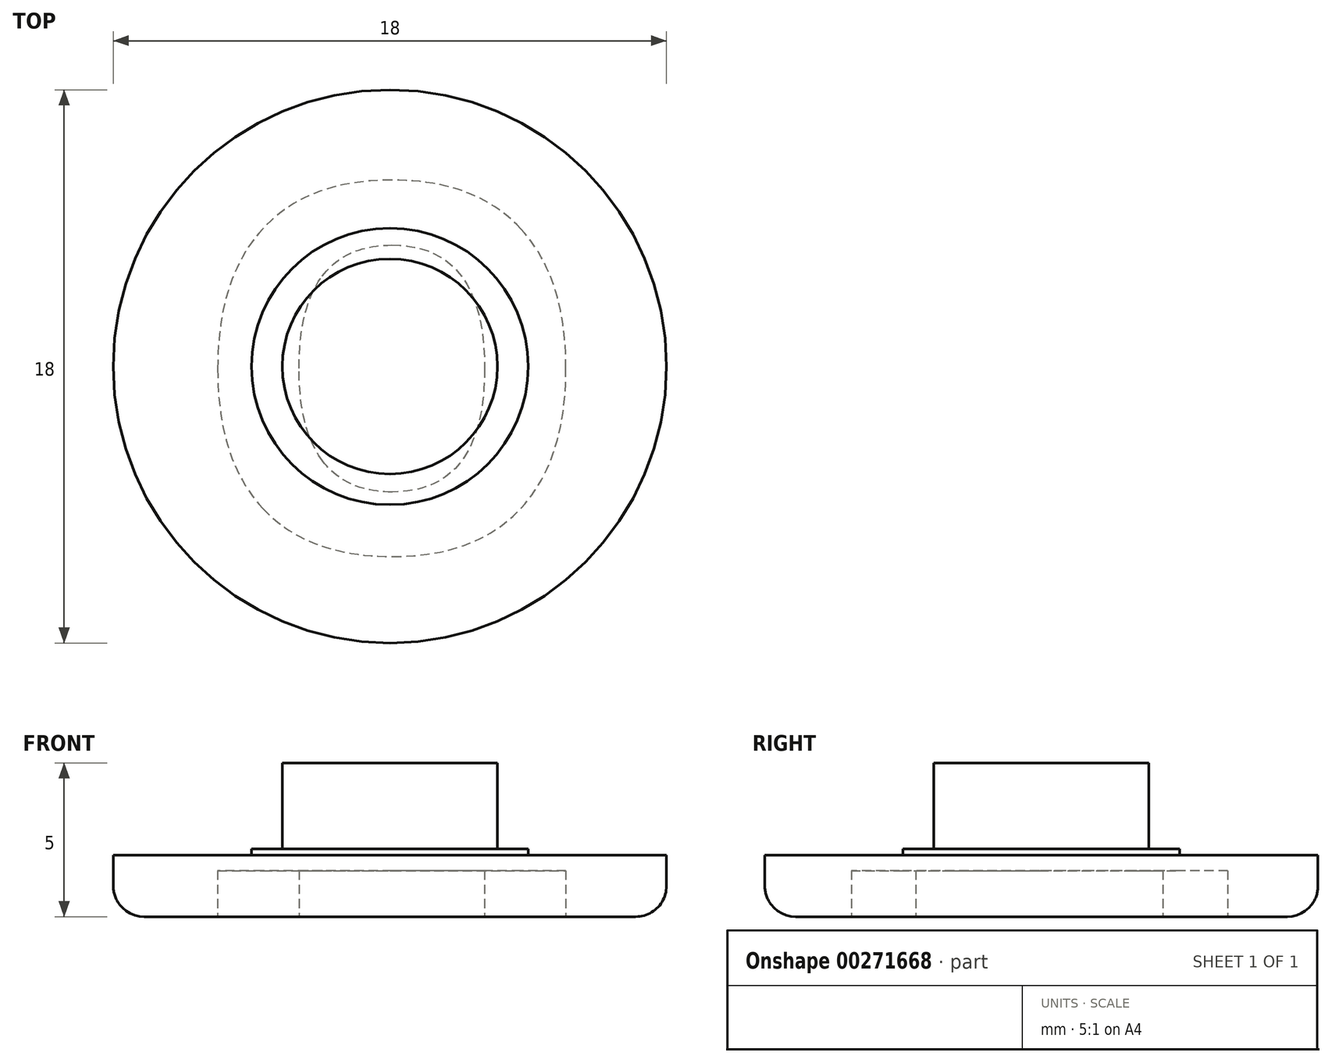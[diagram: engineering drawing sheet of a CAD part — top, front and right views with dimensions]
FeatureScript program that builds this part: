
annotation { "Feature Type Name" : "Feature", "Feature Type Description" : "" }
export const myFeature = defineFeature(function(context is Context, id is Id, definition is map)
    precondition{}
    {
        {
            var Q0;
            Q0=qCreatedBy(makeId("Top.planeOp"),FACE);
            var sketch = newSketch(context, id + "F0", { "sketchPlane" : qUnion([Q0])});
            skCircle(sketch, "E0", {"center": v(0, 0) * mm, "radius": 9 * mm});
            skSolve(sketch);
        }
        {
            var Q0;
            Q0=makeQuery(id+"F0.imprint","IMPRINT",FACE,{"disambiguationData":[TD([[makeQuery(id+"F0.imprint","IMPRINT",EDGE,{"derivedFrom":sQuery(id+"F0.wireOp",EDGE,"E0")}),1.0]])]});
            extrude(context, id + "F1", {"entities" : qUnion([Q0]), "depth" : 2 * mm});
        }
        {
            var Q0;
            Q0=makeQuery(id+"F1.opExtrude","CAP_FACE",FACE,{"disambiguationData":[OSD([sQuery(id+"F0.wireOp",EDGE,"E0")])],"isStart":false});
            var sketch = newSketch(context, id + "F2", { "sketchPlane" : qUnion([Q0])});
            skCircle(sketch, "E1", {"center": v(0, 0) * mm, "radius": 3.5 * mm});
            skSolve(sketch);
        }
        {
            var Q0;
            Q0=makeQuery(id+"F2.imprint","IMPRINT",FACE,{"disambiguationData":[TD([[makeQuery(id+"F2.imprint","IMPRINT",EDGE,{"derivedFrom":sQuery(id+"F2.wireOp",EDGE,"E1")}),1.0]])]});
            extrude(context, id + "F3", {"entities" : qUnion([Q0]), "operationType" : NewBodyOperationType.ADD, "depth" : 3 * mm});
        }
        {
            var Q0;
            Q0=makeQuery(id+"F1.opExtrude","CAP_EDGE",EDGE,{"disambiguationData":[OSD([sQuery(id+"F0.wireOp",EDGE,"E0")])],"isStart":true});
            fillet(context, id + "F4", {"entities" : qUnion([Q0]), "radius" : 1 * mm, "tangentPropagation" : true, "allowEdgeOverflow" : false});
        }
        {
            var Q0;
            Q0=makeQuery(id+"F1.opExtrude","CAP_FACE",FACE,{"disambiguationData":[OSD([sQuery(id+"F0.wireOp",EDGE,"E0")])],"isStart":true});
            var sketch = newSketch(context, id + "F5", { "sketchPlane" : qUnion([Q0])});
            skText(sketch, "E2", { "text": "O", "fontName": "OpenSans-Bold.ttf"});
            const initialGuessF5  = {"E2": [-0.00657, -0.0059, 1, 0, 0.012]};
            skSetInitialGuess(sketch, initialGuessF5);
            skSolve(sketch);
        }
        {
            var Q0;
            Q0=qSketchRegion(id+"F5",true);
            extrude(context, id + "F6", {"entities" : qUnion([Q0]), "operationType" : NewBodyOperationType.REMOVE, "oppositeDirection" : true, "depth" : 1.5 * mm});
        }
        {
            var Q0;
            Q0=makeQuery(id+"F1.opExtrude","CAP_FACE",FACE,{"disambiguationData":[OSD([sQuery(id+"F0.wireOp",EDGE,"E0")])],"isStart":false});
            var sketch = newSketch(context, id + "F7", { "sketchPlane" : qUnion([Q0])});
            skCircle(sketch, "E3", {"center": v(0, 0) * mm, "radius": 4.5 * mm});
            skSolve(sketch);
        }
        {
            var Q0;
            Q0=makeQuery(id+"F7.imprint","IMPRINT",FACE,{"disambiguationData":[TD([[makeQuery(id+"F7.imprint","IMPRINT",EDGE,{"derivedFrom":sQuery(id+"F7.wireOp",EDGE,"E3")}),1.0]])]});
            extrude(context, id + "F8", {"entities" : qUnion([Q0]), "operationType" : NewBodyOperationType.ADD, "depth" : .2 * mm});
        }
    });
